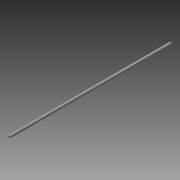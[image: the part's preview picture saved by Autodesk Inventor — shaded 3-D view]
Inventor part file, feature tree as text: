
AUTODESK INVENTOR PART (.ipt)
format: ipt  version: 2015 SP1 (Build 190203100, 203)  size: 107,520 bytes
history: native  units: in
note: dims shown in document units (in); Inventor stores cm internally (conversion verified against a paired STEP export)
features: extrude x2, sketch x2
ambient origin geometry x8: Origin, YZ Plane, XZ Plane, XY Plane, X Axis, Y Axis, Z Axis, Center Point
bodies: Solid1 (feature_tree)
feature tree (4):
  extrude  "Extrusion1"  Depth=0.9843in
  extrude  "Extrusion2"  Depth=83.8583in TaperAngle=0.0deg
  sketch  "Sketch2"  dims[d0=0.9843in d1=0.9843in]
  sketch  "Sketch3"  dims[d3=0.1181in d4=83.8583in d5=0.0in d6=0.2756in d7=0.4331in d8=0.7087in d9=19.3307in d10=0.9843in d11=0.9843in d12=40.9449in d13=0.7087in d14=19.3307in d16=0.0in d17=0.0in]
